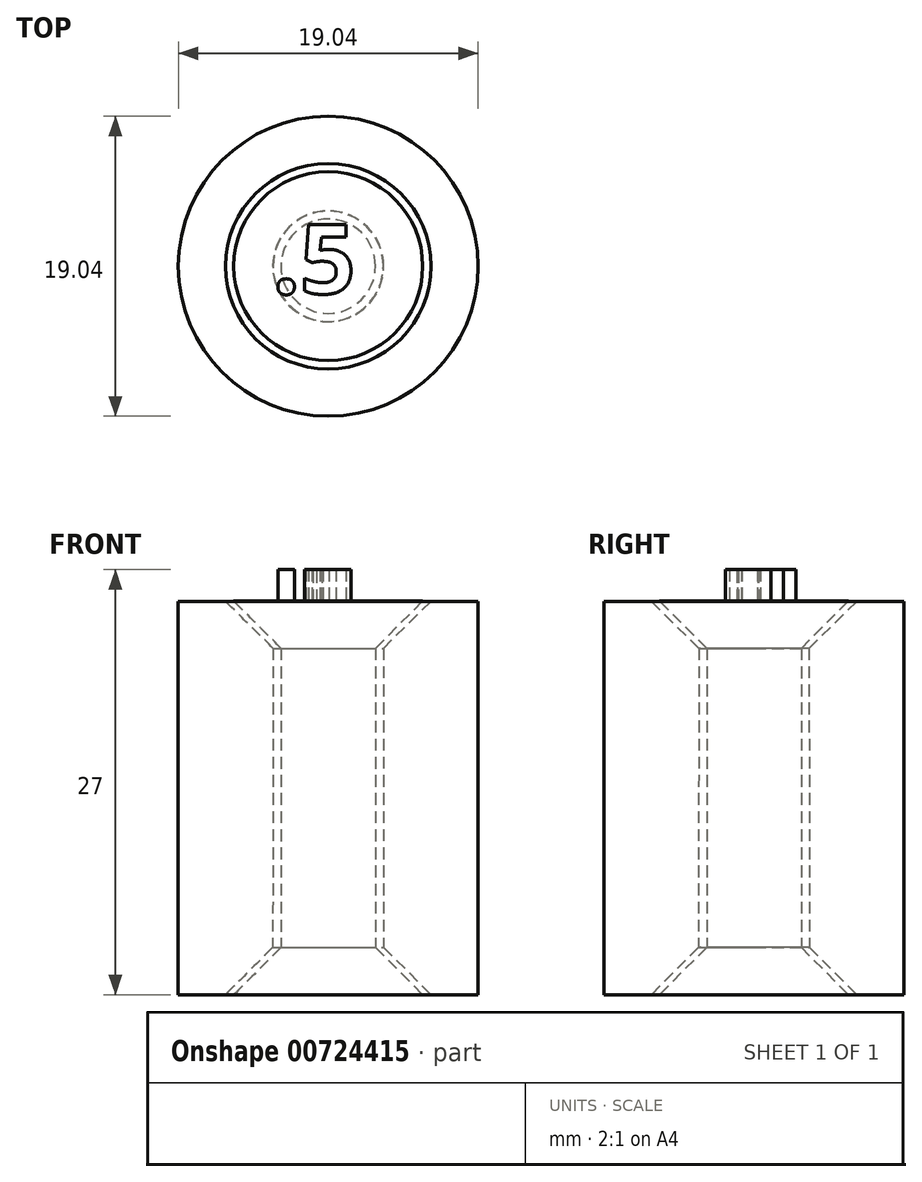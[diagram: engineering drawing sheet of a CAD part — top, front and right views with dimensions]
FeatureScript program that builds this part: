
annotation { "Feature Type Name" : "Feature", "Feature Type Description" : "" }
export const myFeature = defineFeature(function(context is Context, id is Id, definition is map)
    precondition{}
    {
        {
            var Q0;
            Q0=qCreatedBy(makeId("Front.planeOp"),FACE);
            var sketch = newSketch(context, id + "F0", { "sketchPlane" : qUnion([Q0])});
            skLineSegment(sketch, "E0", {"start": v(0, 25) * mm, "end": v(6, 25) * mm});
            skLineSegment(sketch, "E1", {"start": v(0, 0) * mm, "end": v(6, 0) * mm});
            skLineSegment(sketch, "E2", {"start": v(0, 0) * mm, "end": v(0, 3) * mm});
            skLineSegment(sketch, "E3", {"start": v(0, 3) * mm, "end": v(0, 22) * mm});
            skLineSegment(sketch, "E4", {"start": v(0, 22) * mm, "end": v(0, 25) * mm});
            skLineSegment(sketch, "E5", {"start": v(3, 22) * mm, "end": v(6, 25) * mm});
            skLineSegment(sketch, "E6", {"start": v(3, 3) * mm, "end": v(6, 0) * mm});
            skLineSegment(sketch, "E7", {"start": v(3, 22) * mm, "end": v(3, 3) * mm});
            skLineSegment(sketch, "E8", {"start": v(3.5, 22) * mm, "end": v(3.52, 3) * mm});
            skLineSegment(sketch, "E9", {"start": v(3.5, 22) * mm, "end": v(6.52, 24.98) * mm});
            skLineSegment(sketch, "E10", {"start": v(3.52, 3) * mm, "end": v(6.52, 0) * mm});
            skLineSegment(sketch, "E11", {"start": v(6.52, 24.98) * mm, "end": v(9.52, 24.98) * mm});
            skLineSegment(sketch, "E12", {"start": v(9.52, 24.98) * mm, "end": v(9.52, 0) * mm});
            skLineSegment(sketch, "E13", {"start": v(9.52, 0) * mm, "end": v(6.52, 0) * mm});
            skSolve(sketch);
        }
        {
            var Q0;
            Q0 = qSketchRegion(id + "F0", true);
            var Q1;
            Q1=sQuery(id+"F0.wireOp",EDGE,"E3");
            revolve(context, id + "F1", {"surfaceOperationType" : NewSurfaceOperationType.NEW, "entities" : qUnion([Q0]), "axis" : qUnion([Q1]), "revolveType" : RevolveType.FULL});
        }
        {
            var Q0;
            Q0=makeQuery(id+"F1.opRevolve","SWEPT_FACE",FACE,{"disambiguationData":[OSD([sQuery(id+"F0.wireOp",EDGE,"E0")])]});
            var sketch = newSketch(context, id + "F2", { "sketchPlane" : qUnion([Q0])});
            skText(sketch, "E14", { "text": ".5", "fontName": "OpenSans-Bold.ttf"});
            const initialGuessF2  = {"E14": [-0.00355, -0.00174, 1, 0, 0.00443]};
            skSetInitialGuess(sketch, initialGuessF2);
            skSolve(sketch);
        }
        {
            var Q0;
            Q0 = qSketchRegion(id + "F2", true);
            extrude(context, id + "F3", {"entities" : qUnion([Q0]), "operationType" : NewBodyOperationType.ADD, "depth" : 2 * mm, "offsetDistance" : 25 * mm});
        }
    });
